# Revit family: bimlib_narujnyeblokisistemakondicionirovaniya_mrv-w_haier
name_source: partatom
category: Оборудование
units: mm (PartAtom-declared; Revit-internal decimal feet)

## family parameters
Всегда вертикально = Да
На основе рабочей плоскости = Нет
Общий = Нет
При загрузке вырезать с полостями = Нет
Размер круглого соединителя = Использовать диаметр
Тип детали = Нормальный
Точка расчета площади = Нет

## types (3) — shared parameters
ADSK_URL документации изделия = https://haierproff.ru
ADSK_URL страницы изделия = https://haierproff.ru
ADSK_Версия Revit = 2017
ADSK_Группирование = VRF-системы MRV-W
ADSK_Единица измерения = шт.
ADSK_Завод-изготовитель = Haier Group
ADSK_Классификация нагрузок = ОВК
ADSK_Количество = 1
ADSK_Количество фаз = 3
ADSK_Коэффициент мощности = 1
ADSK_Масса = 172
ADSK_Напряжение = 400 В
ADSK_Обозначение = MRV-W
ADSK_Размер_Высота = 995 мм
ADSK_Размер_Глубина = 545 мм
ADSK_Размер_Ширина = 775 мм
BL_BIM library = https://bimlib.pro
HG_URL поставщика = https://haierproff.ru
URL = www.haier.com
Диаметр_Воды = 32 мм
Диаметр_Дренаж = 6.35 мм
Диаметр_Масло = 9.52 мм
Заправка хладагента = 2.00 кг
Изготовитель = Haier Group
Работа на обогрев = Нет
Рабочий диапазон воды_Охлаждение-Обогрев = 7 ~ 45
Тип компрессора = DC INV. СПИРАЛ.
Тип хладагента = R410A
Частота тока = 50 Гц
zero-valued in all types: Отметка по умолчанию

## per-type parameters (varying)
| type | ADSK_Код изделия | ADSK_Наименование | ADSK_Наименование краткое | ADSK_Номинальная мощность | ADSK_Полная мощность | ADSK_Расход воздуха | HG_Расход воды | Диаметр_Газ | Диаметр_Жидкость | Звуковая мощность | Звуковое давление | Обогрев_Максимальная потребляемая мощность | Обогрев_Максимальный ток | Обогрев_Номинальная потребляемая мощность | Обогрев_Номинальный ток | Охлаждение_Максимальная потребляемая мощность | Охлаждение_Максимальный ток | Охлаждение_Номинальная потребляемая мощность | Охлаждение_Номинальный ток | Теплопроизводительность | Холодопроизводительность |
| AV08IMWEWA_8HP_HAIER | AV08IMWEWA | Наружный блок VRF-системы кондиционирования MRV-W, 8HP | VRF-системы MRV-W, 8HP | 4500 Вт | 4500 В·А | 12000.0 м³/ч | 1.3 л/с | 19.05 мм | 9.52 мм | 61 | 50 | 13 кВт | 21 А | 4 кВт | 7 А | 13 кВт | 21 А | 5 кВт | 7 А | 25 кВт | 22 кВт |
| AV10IMWEWA_10HP_HAIER | AV10IMWEWA | Наружный блок VRF-системы кондиционирования MRV-W, 10HP | VRF-системы MRV-W, 10HP | 6000 Вт | 6000 В·А | 12000.0 м³/ч | 1.7 л/с | 22.22 мм | 9.52 мм | 62 | 51 | 15 кВт | 24 А | 6 кВт | 9 А | 15 кВт | 24 А | 6 кВт | 10 А | 32 кВт | 28 кВт |
| AV12IMWEWA_12HP_HAIER | AV12IMWEWA | Наружный блок VRF-системы кондиционирования MRV-W, 12HP | VRF-системы MRV-W, 12HP | 7700 Вт | 7700 В·А | 13500.0 м³/ч | 2.0 л/с | 25.4 мм | 12.7 мм | 64 | 53 | 17 кВт | 27 А | 8 кВт | 12 А | 17 кВт | 27 А | 8 кВт | 12 А | 38 кВт | 34 кВт |
